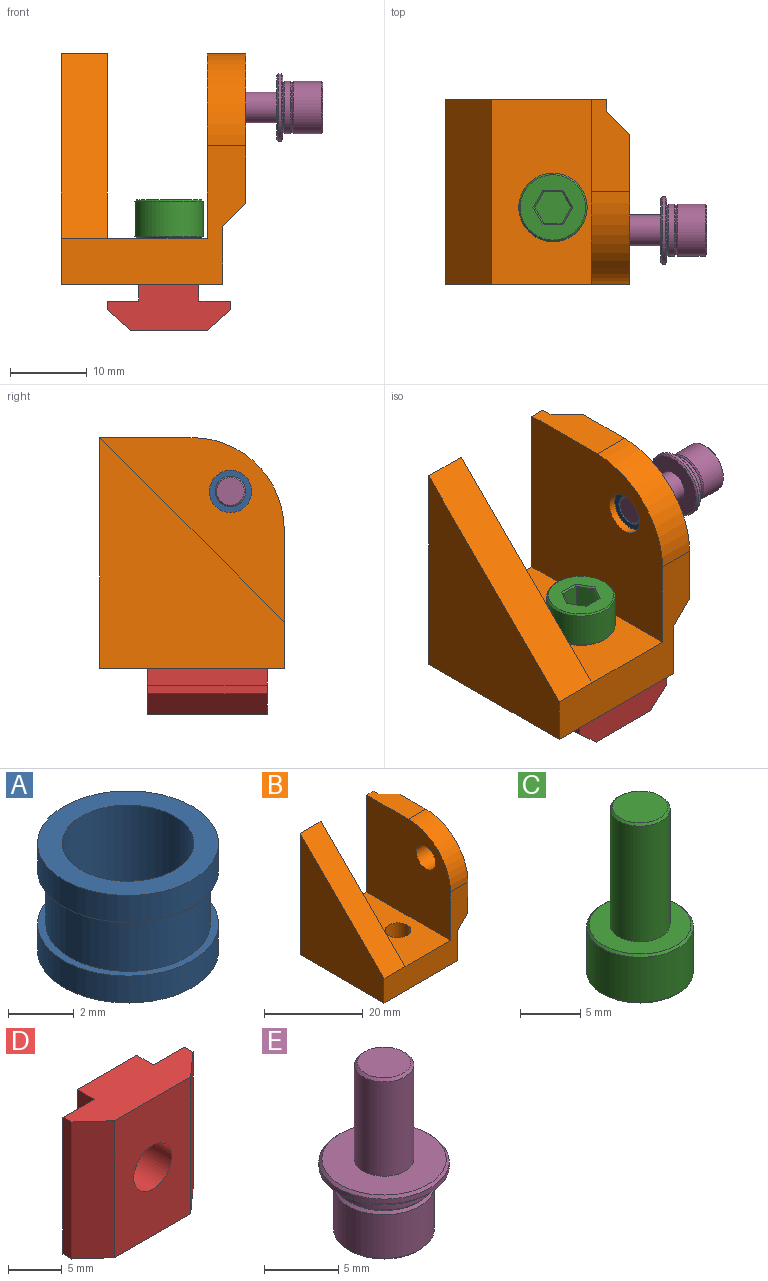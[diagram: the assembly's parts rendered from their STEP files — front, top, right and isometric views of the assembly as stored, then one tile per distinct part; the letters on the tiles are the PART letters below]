
ASSEMBLY  parts=5 mates=4
PART A: 8 faces, bbox 5.5x5.5x4 mm
  f0: cylinder r=2mm len=4mm, axis (0,0,-1), area 50.3mm2, adj f3,f6
  f1: cylinder r=2.75mm len=5.5mm, axis (0,0,-1), area 17.3mm2, adj f2,f3
  f2: plane 5.5x5.5mm, normal (0,0,1), area 4.1mm2, adj f1,f4
  f3: plane 5.5x5.5mm, normal (0,0,-1), area 11.2mm2, adj f0,f1
  f4: cylinder r=2.5mm len=5mm, axis (0,0,-1), area 31.4mm2, adj f2,f7
  f5: cylinder r=2.75mm len=5.5mm, axis (0,0,-1), area 17.3mm2, adj f6,f7
  f6: plane 5.5x5.5mm, normal (0,0,1), area 11.2mm2, adj f0,f5
  f7: plane 5.5x5.5mm, normal (0,0,-1), area 4.1mm2, adj f4,f5
PART B: 17 faces, bbox 24x24x30 mm
  f0: plane 30x24mm, normal (1,0,0), area 217.5mm2, adj f1,f4,f5,f12,f13,f14,f16
  f1: plane 12x5mm, normal (0,0,1), area 51mm2, adj f0,f2,f10,f11,f13,f16
  f2: plane 19.5x19.5mm, normal (1,0,0), area 325.3mm2, adj f1,f5,f10,f12,f13,f14,f15
  f3: plane 24x13mm, normal (0,0,1), area 290.8mm2, adj f5,f7,f9,f11,f16
  f4: plane 24x21mm, normal (0,0,-1), area 482.8mm2, adj f0,f5,f6,f9,f16
  f5: plane 24x18mm, normal (0,-1,0), area 177mm2, adj f0,f2,f3,f4,f6,f8,f10,f11
  f6: plane 30x24mm, normal (-1,0,0), area 432mm2, adj f4,f5,f8,f16
  f7: plane 24x24mm, normal (1,0,0), area 288mm2, adj f3,f8,f16
  f8: plane 24x24mm, normal (0,-0.71,0.71), area 203.6mm2, adj f5,f6,f7,f16
  f9: cylinder r=2.6mm len=6mm, axis (0,0,1), area 98mm2, adj f3,f4
  f10: cylinder r=12mm len=12mm, axis (-1,0,0), area 94.2mm2, adj f1,f2,f5,f11
  f11: plane 24x24mm, normal (-1,0,0), area 521.3mm2, adj f1,f3,f5,f10,f15,f16
  f12: plane 18.3x3mm, normal (0.71,0,-0.71), area 77.6mm2, adj f0,f2,f5,f14
  f13: plane 18.3x3mm, normal (0.71,0.71,0), area 77.6mm2, adj f0,f1,f2,f14
  f14: cone r=1.2mm half-angle=45deg, axis (-1,0,0), area 18mm2, adj f0,f2,f12,f13
  f15: cylinder r=2.75mm len=5.5mm, axis (-1,0,0), area 86.4mm2, adj f2,f11
  f16: plane 30x21mm, normal (0,1,0), area 318mm2, adj f0,f1,f3,f4,f6,f7,f8,f11
PART C: 21 faces, bbox 8.9x8.9x17 mm
  f0: plane 3.8x2.37mm, normal (0,-1,0), area 9mm2, adj f1,f5,f8,f17
  f1: plane 3.8x2.05mm, normal (-0.87,-0.5,0), area 9mm2, adj f0,f2,f8,f18
  f2: plane 3.8x2.05mm, normal (-0.87,0.5,0), area 9mm2, adj f1,f3,f8,f16
  f3: plane 3.8x2.37mm, normal (0,1,0), area 9mm2, adj f2,f4,f8,f14
  f4: plane 3.8x2.05mm, normal (0.87,0.5,0), area 9mm2, adj f3,f5,f8,f13
  f5: plane 3.8x2.05mm, normal (0.87,-0.5,0), area 9mm2, adj f0,f4,f8,f15
  f6: cylinder r=4.45mm len=8.9mm, axis (0,0,-1), area 128.6mm2, adj f12,f19
  f7: plane 8.5x8.5mm, normal (0,0,-1), area 39.2mm2, adj f13,f14,f15,f16,f17,f18,f19
  f8: plane 4.73x4.1mm, normal (0,0,-1), area 14.6mm2, adj f0,f1,f2,f3,f4,f5
  f9: plane 8.5x8.5mm, normal (0,0,1), area 37.1mm2, adj f10,f12
  f10: cylinder r=2.5mm len=11.8mm, axis (0,0,-1), area 185.4mm2, adj f9,f20
  f11: plane 4.6x4.6mm, normal (0,0,1), area 16.6mm2, adj f20
  f12: cone r=4.25mm half-angle=45deg, axis (0,0,-1), area 7.7mm2, adj f6,f9
  f13: plane 2.25x1.41mm, normal (0.61,0.35,-0.71), area 0.7mm2, adj f4,f7,f14,f15
  f14: plane 2.6x0.2mm, normal (0,0.71,-0.71), area 0.7mm2, adj f3,f7,f13,f16
  f15: plane 2.25x1.41mm, normal (0.61,-0.35,-0.71), area 0.7mm2, adj f5,f7,f13,f17
  f16: plane 2.25x1.41mm, normal (-0.61,0.35,-0.71), area 0.7mm2, adj f2,f7,f14,f18
  f17: plane 2.6x0.2mm, normal (0,-0.71,-0.71), area 0.7mm2, adj f0,f7,f15,f18
  f18: plane 2.25x1.41mm, normal (-0.61,-0.35,-0.71), area 0.7mm2, adj f1,f7,f16,f17
  f19: cone r=4.45mm half-angle=45deg, axis (0,0,1), area 7.7mm2, adj f6,f7
  f20: cone r=2.3mm half-angle=45deg, axis (0,0,-1), area 4.3mm2, adj f10,f11
PART D: 13 faces, bbox 16x6x15.6 mm
  f0: plane 15.6x2.2mm, normal (1,0,0), area 34.3mm2, adj f1,f9,f10,f11
  f1: plane 15.6x7.8mm, normal (0,1,0), area 102mm2, adj f0,f2,f10,f11,f12
  f2: plane 15.6x2.2mm, normal (-1,0,0), area 34.3mm2, adj f1,f3,f10,f11
  f3: plane 15.6x4.1mm, normal (0,1,0), area 64mm2, adj f2,f4,f10,f11
  f4: plane 15.6x1.1mm, normal (-1,0,0), area 17.2mm2, adj f3,f5,f10,f11
  f5: plane 15.6x3mm, normal (-0.67,-0.74,0), area 63mm2, adj f4,f6,f10,f11
  f6: plane 15.6x10mm, normal (0,-1,0), area 136.4mm2, adj f5,f7,f10,f11,f12
  f7: plane 15.6x3mm, normal (0.67,-0.74,0), area 63mm2, adj f6,f8,f10,f11
  f8: plane 15.6x1.1mm, normal (1,0,0), area 17.2mm2, adj f7,f9,f10,f11
  f9: plane 15.6x4.1mm, normal (0,1,0), area 64mm2, adj f0,f8,f10,f11
  f10: plane 16x6mm, normal (0,0,1), area 69.9mm2, adj f0,f1,f2,f3,f4,f5,f6,f7
  f11: plane 16x6mm, normal (0,0,-1), area 69.9mm2, adj f0,f1,f2,f3,f4,f5,f6,f7
  f12: cylinder r=2.5mm len=6mm, axis (0,1,0), area 94.2mm2, adj f1,f6
PART E: 28 faces, bbox 8.8x8.8x14 mm
  f0: plane 3.05x1.79mm, normal (0,1,0), area 5.5mm2, adj f1,f5,f8,f13
  f1: plane 3.05x1.55mm, normal (-0.87,0.5,0), area 5.5mm2, adj f0,f2,f8,f14
  f2: plane 3.05x1.55mm, normal (-0.87,-0.5,0), area 5.5mm2, adj f1,f3,f8,f12
  f3: plane 3.05x1.79mm, normal (0,-1,0), area 5.5mm2, adj f2,f4,f8,f10
  f4: plane 3.05x1.55mm, normal (0.87,-0.5,0), area 5.5mm2, adj f3,f5,f8,f9
  f5: plane 3.05x1.55mm, normal (0.87,0.5,0), area 5.5mm2, adj f0,f4,f8,f11
  f6: cylinder r=3.4mm len=6.8mm, axis (0,0,-1), area 76.9mm2, adj f15,f16
  f7: plane 6.4x6.4mm, normal (0,0,-1), area 21.6mm2, adj f9,f10,f11,f12,f13,f14,f15
  f8: plane 3.58x3.1mm, normal (0,0,-1), area 8.3mm2, adj f0,f1,f2,f3,f4,f5
  f9: plane 1.75x1.13mm, normal (0.61,-0.35,-0.71), area 0.5mm2, adj f4,f7,f10,f11
  f10: plane 2.02x0.2mm, normal (0,-0.71,-0.71), area 0.5mm2, adj f3,f7,f9,f12
  f11: plane 1.75x1.13mm, normal (0.61,0.35,-0.71), area 0.5mm2, adj f5,f7,f9,f13
  f12: plane 1.75x1.13mm, normal (-0.61,-0.35,-0.71), area 0.5mm2, adj f2,f7,f10,f14
  f13: plane 2.02x0.2mm, normal (0,0.71,-0.71), area 0.5mm2, adj f0,f7,f11,f14
  f14: plane 1.75x1.13mm, normal (-0.61,0.35,-0.71), area 0.5mm2, adj f1,f7,f12,f13
  f15: cone r=3.4mm half-angle=45deg, axis (0,0,1), area 5.9mm2, adj f6,f7
  f16: cone r=3.2mm half-angle=45deg, axis (0,0,-1), area 5.9mm2, adj f6,f18
  f17: cylinder r=3.4mm len=6.8mm, axis (0,0,-1), area 17.1mm2, adj f18,f19
  f18: cone r=3.4mm half-angle=45deg, axis (0,0,1), area 5.9mm2, adj f16,f17
  f19: cone r=3.2mm half-angle=45deg, axis (0,0,-1), area 5.9mm2, adj f17,f22
  f20: cylinder r=4.4mm len=8.8mm, axis (0,0,-1), area 11.1mm2, adj f26,f27
  f21: plane 8.4x8.4mm, normal (0,0,1), area 42.9mm2, adj f25,f26
  f22: plane 8.4x8.4mm, normal (0,0,-1), area 23.2mm2, adj f19,f27
  f23: plane 3.6x3.6mm, normal (0,0,1), area 10.2mm2, adj f24
  f24: cone r=1.8mm half-angle=45deg, axis (0,0,-1), area 3.4mm2, adj f23,f25
  f25: cylinder r=2mm len=7.8mm, axis (0,0,-1), area 98mm2, adj f21,f24
  f26: cone r=4.2mm half-angle=45deg, axis (0,0,-1), area 7.6mm2, adj f20,f21
  f27: cone r=4.4mm half-angle=45deg, axis (0,0,1), area 7.6mm2, adj f20,f22
PLACE A rot(axis=(0.71,0,0.71),180deg) t=(28.51,-18.82,53.28)mm
PLACE B t=(-100.43,-0.58,-1.08)mm
PLACE C rot(axis=(1,0,0),180deg) t=(-10.21,17.5,9.92)mm
PLACE D rot(axis=(1,0,0),90deg) t=(75.07,17.22,24.89)mm
PLACE E rot(axis=(0.71,0,-0.71),180deg) t=(42.51,-1.67,44.64)mm
MATE fastened A.f0 <-> B.f15  axis (1,0,0) through (32.51,6.42,21.92)mm
MATE fastened C.f6 <-> B.f9  axis (0,0,-1) through (22.51,9.42,4.92)mm
MATE fastened E.f6 <-> B.f15  axis (-1,0,0) through (28.51,6.42,21.92)mm
MATE fastened D.f12 <-> C.f6  axis (0,0,1) through (22.51,9.42,-1.08)mm
